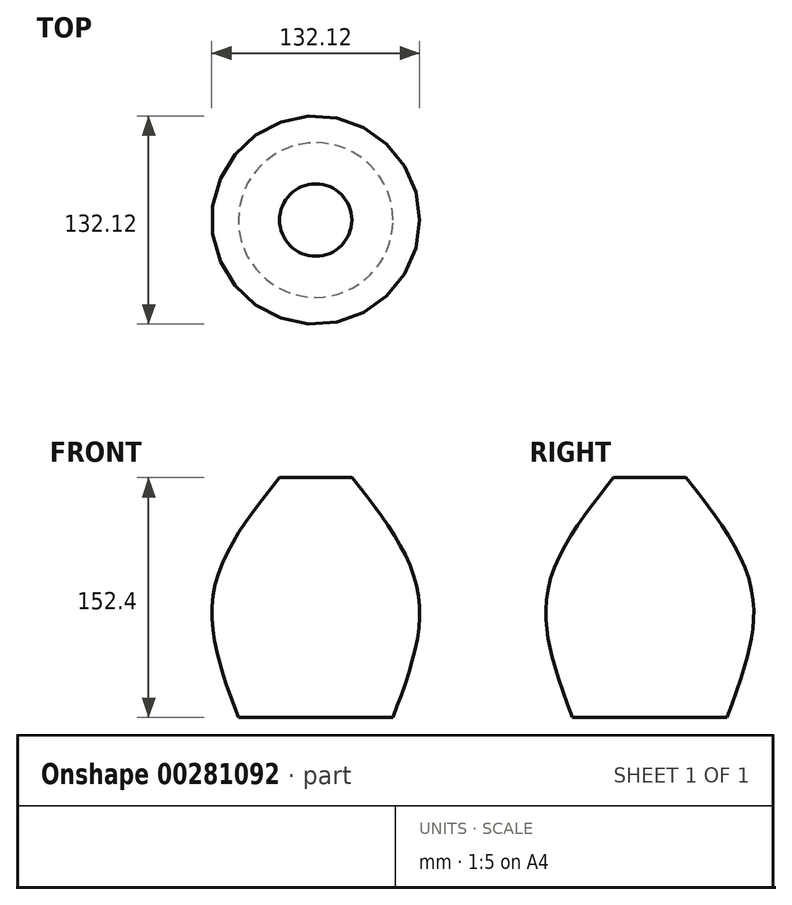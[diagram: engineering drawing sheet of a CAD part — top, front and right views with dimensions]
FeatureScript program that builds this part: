
annotation { "Feature Type Name" : "Feature", "Feature Type Description" : "" }
export const myFeature = defineFeature(function(context is Context, id is Id, definition is map)
    precondition{}
    {
        {
            var Q0;
            Q0=qCreatedBy(makeId("Top.planeOp"),FACE);
            cPlane(context, id + "F0", {"entities" : qUnion([Q0]), "cplaneType" : CPlaneType.OFFSET, "offset" : 76.2 * mm, "width" : 152.4 * mm, "height" : 152.4 * mm});
        }
        {
            var Q0;
            Q0=qCreatedBy(makeId("Top.planeOp"),FACE);
            cPlane(context, id + "F1", {"entities" : qUnion([Q0]), "cplaneType" : CPlaneType.OFFSET, "offset" : 76.2 * mm, "oppositeDirection" : true, "width" : 152.4 * mm, "height" : 152.4 * mm});
        }
        {
            var Q0;
            Q0=qCreatedBy(makeId("Top.planeOp"),FACE);
            var sketch = newSketch(context, id + "F2", { "sketchPlane" : qUnion([Q0])});
            skCircle(sketch, "E0", {"center": v(0, 0) * mm, "radius": 65.48 * mm});
            skSolve(sketch);
        }
        {
            var Q0;
            Q0=qCreatedBy(id+"F0.planeOp",FACE);
            var sketch = newSketch(context, id + "F3", { "sketchPlane" : qUnion([Q0])});
            skCircle(sketch, "E1", {"center": v(0, 0) * mm, "radius": 22.97 * mm});
            skSolve(sketch);
        }
        {
            var Q0;
            Q0=qCreatedBy(id+"F1.planeOp",FACE);
            var sketch = newSketch(context, id + "F4", { "sketchPlane" : qUnion([Q0])});
            skCircle(sketch, "E2", {"center": v(0, 0) * mm, "radius": 49.09 * mm});
            skSolve(sketch);
        }
        {
            var Q0;
            Q0=makeQuery(id+"F4.imprint","IMPRINT",FACE,{"disambiguationData":[TD([[makeQuery(id+"F4.imprint","IMPRINT",EDGE,{"derivedFrom":sQuery(id+"F4.wireOp",EDGE,"E2")}),1.0]])]});
            var Q1;
            Q1=makeQuery(id+"F2.imprint","IMPRINT",FACE,{"disambiguationData":[TD([[makeQuery(id+"F2.imprint","IMPRINT",EDGE,{"derivedFrom":sQuery(id+"F2.wireOp",EDGE,"E0")}),1.0]])]});
            var Q2;
            Q2=makeQuery(id+"F3.imprint","IMPRINT",FACE,{"disambiguationData":[TD([[makeQuery(id+"F3.imprint","IMPRINT",EDGE,{"derivedFrom":sQuery(id+"F3.wireOp",EDGE,"E1")}),1.0]])]});
            loft(context, id + "F5", {"sheetProfilesArray" : [{ "sheetProfileEntities" : qUnion([Q0]) }, { "sheetProfileEntities" : qUnion([Q1]) }, { "sheetProfileEntities" : qUnion([Q2]) }]});
        }
    });
